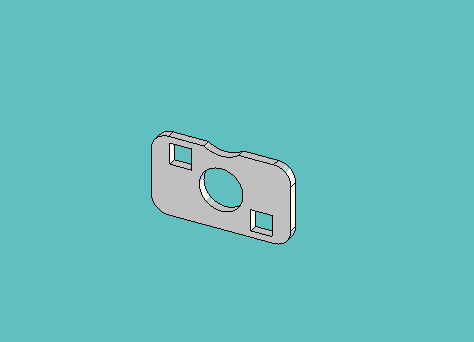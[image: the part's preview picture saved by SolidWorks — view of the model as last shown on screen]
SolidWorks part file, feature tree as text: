
SOLIDWORKS PART (.sldprt)
format: sldprt  version: not decoded by parser v0  size: 339,456 bytes
history: native  units: mm
features: sketch x4, extrude x2, fillet x2, material x1, cut_extrude x1 (+11 scaffold rows collapsed)
feature tree (21):
  scaffold x11  (default folders/planes/origin — collapsed)
  material  "Material <not specified>"
  sketch  "Sketch1"  dims[D1=7.9375mm D2=14.732mm D3=33.3375mm]
  extrude  "Extrude1"  Depth=1.5875mm
  sketch  "Sketch3"  dims[D2=7.9375mm D3=7.9375mm D1=0.0mm]
  extrude  "Extrude2"  Depth=3.175mm
  sketch  "Sketch2"  dims[D1=2.159mm D2=2.159mm D3=11.1125mm D4=3.175mm D5=3.175mm D6=13.589mm D7=13.589mm D8=11.9126mm]
  cut_extrude  "Cut-Extrude1"  [1 undecoded]
  fillet  "Fillet2"  Radius=3.175mm
  fillet  "Fillet1"  Radius=3.175mm
  sketch  "Sketch4"  dims[D1=2.7432mm D2=2.7432mm]
decode coverage: 8 of 9 modeling features carry decoded parameters
note: 1 parameter value undecoded
note: suppression state not decoded; provenance and decode notes live in map.json
